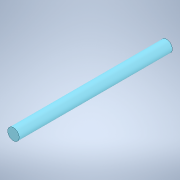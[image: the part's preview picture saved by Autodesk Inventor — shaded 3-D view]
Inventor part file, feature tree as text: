
AUTODESK INVENTOR PART (.ipt)
format: ipt  version: 2022 (Build 260153000, 153)  size: 102,400 bytes
history: native  units: in
note: dims shown in document units (in); Inventor stores cm internally (conversion verified against a paired STEP export)
features: extrude x1, sketch x1
ambient origin geometry x8: Origin, YZ Plane, XZ Plane, XY Plane, X Axis, Y Axis, Z Axis, Center Point
bodies: Solid1 (feature_tree)
feature tree (2):
  extrude  "Extrusion1"  TaperAngle=0.0deg  [1 undecoded]
  sketch  "Sketch2"  dims[d0=3.937in d1=0.0in d2=0.2953in d3=0.0344in d4=0.0197in d5=0.0344in]
note: 1 required parameter value undecoded (feature->parameter linkage not recoverable at this tier; creation-order binding heuristic only, values carry confidence <= 0.55)
